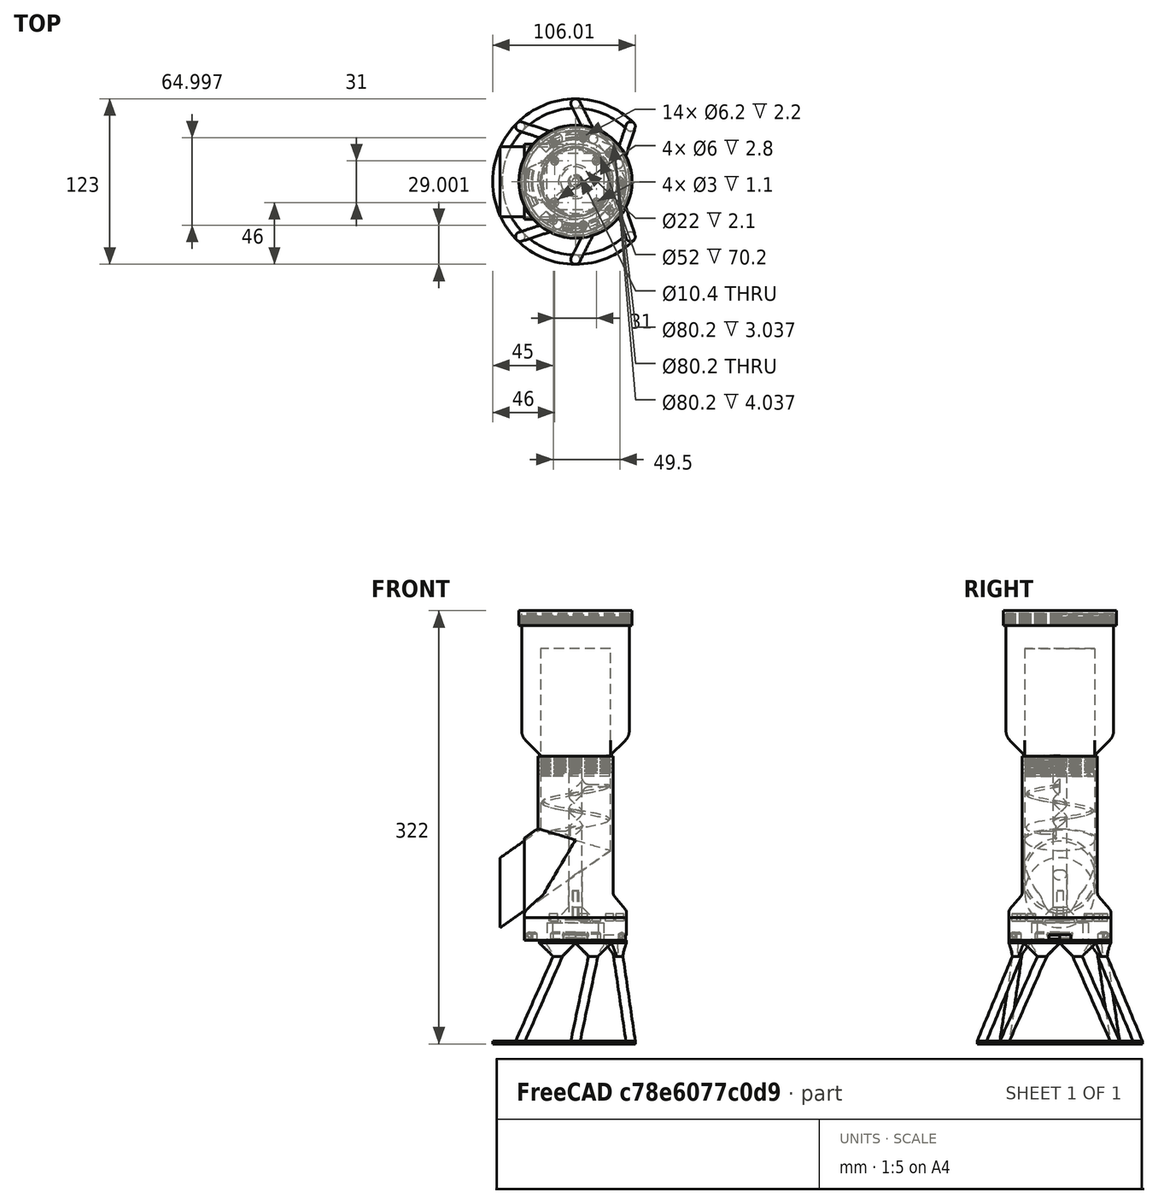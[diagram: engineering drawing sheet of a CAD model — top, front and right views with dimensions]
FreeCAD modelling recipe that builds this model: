
FCSTD DOCUMENT  (FreeCAD 1.0R38806 (Git))
Label: feeder
License: All rights reserved
LicenseURL: http://en.wikipedia.org/wiki/All_rights_reserved
objects: Sketcher::SketchObject×32, PartDesign::SubShapeBinder×25, PartDesign::Pocket×13, PartDesign::Pad×11, PartDesign::Body×8, PartDesign::PolarPattern×5, PartDesign::Revolution×4, PartDesign::Fillet×4, PartDesign::AdditiveHelix×3, PartDesign::Groove×3, PartDesign::SubtractiveHelix×2, Spreadsheet::Sheet×1, PartDesign::Mirrored×1, PartDesign::AdditiveLoft×1, PartDesign::MultiTransform×1, PartDesign::Boolean×1, PartDesign::Chamfer×1
note: 239 computed .brp shape members not serialized (recipe doc carries the construction recipe); baked Part::Feature solids carry a one-line shape summary decoded from their .brp

FEATURE [Spreadsheet::Sheet] Spreadsheet
  cells = A1='worm radius; B1(wormR)==25 mm; A2='wall thickness; B2(wallThickness)==2 mm; A3='worm wall gap; B3(wormWallGap)==1 mm; A4='tolerance; B4(tol)==0.1 mm; A5='shaft radius; B5(shaftR)==5 mm; A6='body radius; B6(bodyR)==wormR + wallThickness + wormWallGap; A7='worm Thickness; B7(wormThickness)==2 mm; A8='worm Smoothness; B8(wormSmoothness)==5 mm; A9='body height; B9(bodyH)==100 mm; A10='exit ratio; B10(exitRatio)=0.7; A11='worm Pitch; B11(wormPitch)==wormR; A12='legRadius; B12(legR)==5 mm; A13='motorMountHeight; B13(mountH)==17 mm; A14='container height; B14(containerH)==120 mm; A15='container radius; B15(containerR)==40 mm
FEATURE [Sketcher::SketchObject] Sketch  label="bodyProfile"
  ArcFitTolerance = 0
  AttachmentSupport = -> [XY_Plane]
  FullyConstrained = true
  MakeInternals = false
  MapMode = 5
  expr: Constraints[6] = Spreadsheet.wallThickness
  expr: Constraints[7] = Spreadsheet.wormR + Spreadsheet.wormWallGap
  sketch-geometry (3):
    g0: Circle CenterX=0 CenterY=0 CenterZ=0 NormalX=0 NormalY=0 NormalZ=1 AngleXU=0 Radius=26
    g1: Circle CenterX=0 CenterY=0 CenterZ=0 NormalX=0 NormalY=0 NormalZ=1 AngleXU=0 Radius=28
    g2: LineSegment [constr] StartX=26 StartY=0 StartZ=0 EndX=28 EndY=0 EndZ=0
  constraints (8):
    c: Coincident(g0,g-1)
    c: Coincident(g1,g0)
    c: PointOnObject(g2,g-1)
    c: PointOnObject(g2,g1)
    c: PointOnObject(g2,g0)
    c: PointOnObject(g2,g-1)
    c: DistanceX(g2,g2) = 2
    c: Radius(g0) = 26
FEATURE [Sketcher::SketchObject] Sketch001  label="wormProfile"
  ArcFitTolerance = 0
  AttachmentSupport = -> [XZ_Plane]
  FullyConstrained = true
  MakeInternals = false
  MapMode = 5
  Placement = pos=(0,0,0) rot=(1,0,0;1.5708rad)
  expr: Constraints[11] = Spreadsheet.wormSmoothness
  expr: Constraints[14] = Spreadsheet.wormR
  expr: Constraints[15] = Spreadsheet.wormThickness
  expr: Constraints[16] = Spreadsheet.shaftR - Spreadsheet.tol
  sketch-geometry (7):
    g0: ArcOfCircle CenterX=9.9 CenterY=6 CenterZ=0 NormalX=0 NormalY=0 NormalZ=1 AngleXU=0 Radius=5 StartAngle=3.1416 EndAngle=4.71239
    g1: LineSegment StartX=9.9 StartY=1 StartZ=0 EndX=24 EndY=1 EndZ=0
    g2: ArcOfCircle CenterX=24 CenterY=0 CenterZ=0 NormalX=0 NormalY=0 NormalZ=1 AngleXU=0 Radius=1 StartAngle=4.71239 EndAngle=7.85398
    g3: LineSegment StartX=24 StartY=-1 StartZ=0 EndX=9.9 EndY=-1 EndZ=0
    g4: ArcOfCircle CenterX=9.9 CenterY=-6 CenterZ=0 NormalX=0 NormalY=0 NormalZ=1 AngleXU=0 Radius=5 StartAngle=1.5708 EndAngle=3.14159
    g5: LineSegment StartX=4.9 StartY=5.99998 StartZ=0 EndX=4.9 EndY=-6 EndZ=0
    g6: GeomPoint [constr] X=25 Y=0 Z=0
  constraints (18):
    c: Horizontal(g1)
    c: Horizontal(g3)
    c: Coincident(g5,g0)
    c: Vertical(g5)
    c: Tangent(g5,g0)
    c: PointOnObject(g2,g-1)
    c: Tangent(g2,g1) = 1.5708
    c: Tangent(g3,g2) = 1.5708
    c: Tangent(g1,g0) = -1.5708
    c: Tangent(g4,g3) = -1.5708
    c: Equal(g0,g4)
    c: Radius(g0) = 5
    c: PointOnObject(g6,g2)
    c: PointOnObject(g6,g-1)
    c: DistanceX(g-1,g6) = 25
    c: DistanceY(g2,g1) = 2
    c: DistanceX(g-1,g0) = 4.9
    c: Tangent(g5,g4) = -1.5708
FEATURE [PartDesign::SubShapeBinder] Binder
  BindCopyOnChange = 0
  BindMode = 0
  ClaimChildren = false
  Context = -> Body001 [Binder.]
  Fuse = false
  MakeFace = true
  OffsetFill = false
  OffsetIntersection = false
  OffsetJoinType = 0
  OffsetOpenResult = false
  PartialLoad = false
  Relative = true
  Support = -> [Body[Sketch.Edge2]]
  _Version = 2
FEATURE [Sketcher::SketchObject] Sketch004  label="wormShaftProfile"
  ArcFitTolerance = 0
  AttachmentSupport = -> [XY_Plane]
  FullyConstrained = true
  MakeInternals = false
  MapMode = 5
  expr: Constraints[1] = Spreadsheet.shaftR
  expr: Constraints[7] = Spreadsheet.tol
  sketch-geometry (3):
    g0: Circle CenterX=0 CenterY=0 CenterZ=0 NormalX=0 NormalY=0 NormalZ=1 AngleXU=0 Radius=5
    g1: Circle CenterX=0 CenterY=0 CenterZ=0 NormalX=0 NormalY=0 NormalZ=1 AngleXU=0 Radius=5.1
    g2: LineSegment [constr] StartX=5 StartY=0 StartZ=0 EndX=5.1 EndY=0 EndZ=0
  constraints (8):
    c: Coincident(g0,g-1)
    c: Radius(g0) = 5
    c: Coincident(g1,g0)
    c: PointOnObject(g2,g0)
    c: PointOnObject(g2,g1)
    c: PointOnObject(g2,g-1)
    c: PointOnObject(g2,g-1)
    c: DistanceX(g2,g2) = 0.1
FEATURE [PartDesign::SubShapeBinder] Binder005
  BindCopyOnChange = 0
  BindMode = 0
  ClaimChildren = false
  Context = -> Body002 [Binder005.]
  Fuse = false
  MakeFace = true
  OffsetFill = false
  OffsetIntersection = false
  OffsetJoinType = 0
  OffsetOpenResult = false
  PartialLoad = false
  Placement = pos=(0,0,98) rot=(0,0,1;0rad)
  Relative = true
  Support = -> [Body[Sketch001.]]
  _Version = 2
  expr: .Placement.Base.z = Spreadsheet.bodyH + 10 mm - Spreadsheet.wormThickness - Spreadsheet.wormSmoothness - 5 mm
FEATURE [PartDesign::SubShapeBinder] Binder006
  BindCopyOnChange = 0
  BindMode = 0
  ClaimChildren = false
  Context = -> Body002 [Binder006.]
  Fuse = false
  MakeFace = true
  OffsetFill = false
  OffsetIntersection = false
  OffsetJoinType = 0
  OffsetOpenResult = false
  PartialLoad = false
  Relative = true
  Support = -> [Body[Sketch004.Edge1]]
  _Version = 2
FEATURE [PartDesign::Pad] Pad001
  Direction = (0,0,1)
  Length = 120
  Length2 = 10
  Profile = -> Binder006
  Suppressed = false
  Type = 0
  expr: Length = Spreadsheet.bodyH + 20 mm
FEATURE [PartDesign::AdditiveHelix] AdditiveHelix
  Angle = 0
  Axis = (1e-16,1e-16,1)
  Base = (0,0,0)
  BaseFeature = -> Pad001
  Growth = 0
  HasBeenEdited = true
  Height = 35
  LeftHanded = false
  Mode = 0
  Outside = false
  Pitch = 25
  Profile = -> Binder005 [Face1]
  ReferenceAxis = -> Z_Axis002
  Reversed = true
  Suppressed = false
  Turns = 1.4
  expr: Height = Spreadsheet.bodyH - 2 * Spreadsheet.bodyR - Spreadsheet.wormSmoothness - 2 * Spreadsheet.wormThickness
  expr: Pitch = Spreadsheet.wormPitch
FEATURE [Sketcher::SketchObject] Sketch073  label="Nema17"
  ArcFitTolerance = 0
  AttachmentSupport = -> [XY_Plane]
  FullyConstrained = true
  MakeInternals = false
  MapMode = 5
  sketch-geometry (21):
    g0: LineSegment StartX=-17 StartY=21.15 StartZ=0 EndX=17 EndY=21.15 EndZ=0
    g1: LineSegment StartX=17 StartY=21.15 StartZ=0 EndX=21.15 EndY=17 EndZ=0
    g2: LineSegment StartX=21.15 StartY=17 StartZ=0 EndX=21.15 EndY=-17 EndZ=0
    g3: LineSegment StartX=21.15 StartY=-17 StartZ=0 EndX=17 EndY=-21.15 EndZ=0
    g4: LineSegment StartX=17 StartY=-21.15 StartZ=0 EndX=-17 EndY=-21.15 EndZ=0
    g5: LineSegment StartX=-17 StartY=-21.15 StartZ=0 EndX=-21.15 EndY=-17 EndZ=0
    g6: LineSegment StartX=-21.15 StartY=-17 StartZ=0 EndX=-21.15 EndY=17 EndZ=0
    g7: LineSegment StartX=-21.15 StartY=17 StartZ=0 EndX=-17 EndY=21.15 EndZ=0
    g8: Circle CenterX=15.5 CenterY=15.5 CenterZ=0 NormalX=0 NormalY=0 NormalZ=1 AngleXU=0 Radius=1.5
    g9: Circle CenterX=-15.5 CenterY=15.5 CenterZ=0 NormalX=0 NormalY=0 NormalZ=1 AngleXU=0 Radius=1.5
    g10: Circle CenterX=-15.5 CenterY=-15.5 CenterZ=0 NormalX=0 NormalY=0 NormalZ=1 AngleXU=0 Radius=1.5
    g11: Circle CenterX=15.5 CenterY=-15.5 CenterZ=0 NormalX=0 NormalY=0 NormalZ=1 AngleXU=0 Radius=1.5
    g12: LineSegment [constr] StartX=-15.5 StartY=15.5 StartZ=0 EndX=-15.5 EndY=-15.5 EndZ=0
    g13: LineSegment [constr] StartX=-15.5 StartY=-15.5 StartZ=0 EndX=15.5 EndY=-15.5 EndZ=0
    g14: LineSegment [constr] StartX=15.5 StartY=-15.5 StartZ=0 EndX=15.5 EndY=15.5 EndZ=0
    g15: LineSegment [constr] StartX=15.5 StartY=15.5 StartZ=0 EndX=-15.5 EndY=15.5 EndZ=0
    g16: GeomPoint [constr] X=0 Y=0 Z=0
    g17: Circle CenterX=0 CenterY=0 CenterZ=0 NormalX=0 NormalY=0 NormalZ=1 AngleXU=0 Radius=11
    g18: Circle CenterX=0 CenterY=0 CenterZ=0 NormalX=0 NormalY=0 NormalZ=1 AngleXU=0 Radius=2.5
    g19: LineSegment StartX=-1.44513 StartY=-2.04 StartZ=0 EndX=1.44513 EndY=-2.04 EndZ=0
    g20: GeomPoint [constr] X=0 Y=2.5 Z=0
  constraints (48):
    c: Coincident(g0,g1)
    c: Coincident(g1,g2)
    c: Coincident(g2,g3)
    c: Coincident(g3,g4)
    c: Coincident(g4,g5)
    c: Coincident(g5,g6)
    c: Coincident(g6,g7)
    c: Coincident(g7,g0)
    c: Equal(g0,g6)
    c: DistanceX(g6,g1) = 42.3
    c: DistanceY(g4,g0) = 42.3
    c: Symmetric(g3,g0,g-1)
    c: Symmetric(g1,g2,g-1)
    c: Symmetric(g0,g0,g-2)
    c: Symmetric(g6,g1,g-2)
    c: DistanceX(g0,g0) = 34
    c: Symmetric(g2,g5,g-2)
    c: Symmetric(g3,g4,g-2)
    c: Coincident(g12,g13)
    c: Coincident(g13,g14)
    c: Coincident(g14,g15)
    c: Coincident(g15,g12)
    c: Horizontal(g13)
    c: Horizontal(g15)
    c: Vertical(g12)
    c: Vertical(g14)
    c: Symmetric(g13,g12,g16)
    c: Coincident(g16,g-1)
    c: Equal(g15,g14)
    c: DistanceX(g15,g15) = 31
    c: Coincident(g8,g14)
    c: Coincident(g9,g12)
    c: Coincident(g11,g13)
    c: Coincident(g10,g12)
    c: Equal(g8,g11)
    c: Equal(g11,g10)
    c: Equal(g10,g9)
    c: Diameter(g8) = 3
    c: Coincident(g17,g16)
    c: Coincident(g18,g17)
    c: Diameter(g17) = 22
    c: Diameter(g18) = 5
    c: PointOnObject(g19,g18)
    c: PointOnObject(g19,g18)
    c: Horizontal(g19)
    c: PointOnObject(g20,g18)
    c: PointOnObject(g20,g-2)
    c: DistanceY(g19,g20) = 4.54
FEATURE [PartDesign::SubShapeBinder] Binder021
  BindCopyOnChange = 0
  BindMode = 0
  ClaimChildren = false
  Context = -> Body005 [Binder021.]
  Fuse = false
  MakeFace = true
  OffsetFill = false
  OffsetIntersection = false
  OffsetJoinType = 0
  OffsetOpenResult = false
  PartialLoad = false
  Relative = true
  Support = -> [Body[Sketch073.]]
  _Version = 2
FEATURE [PartDesign::SubShapeBinder] Binder024
  BindCopyOnChange = 0
  BindMode = 0
  ClaimChildren = false
  Context = -> Body005 [Binder024.]
  Fuse = false
  MakeFace = true
  OffsetFill = false
  OffsetIntersection = false
  OffsetJoinType = 0
  OffsetOpenResult = false
  PartialLoad = false
  Placement = pos=(0,0,-2) rot=(0,0,1;0rad)
  Relative = true
  Support = -> [Binder021[Edge13]]
  _Version = 2
FEATURE [PartDesign::SubShapeBinder] Binder025
  BindCopyOnChange = 0
  BindMode = 0
  ClaimChildren = false
  Context = -> Body005 [Binder025.]
  Fuse = false
  MakeFace = true
  OffsetFill = false
  OffsetIntersection = false
  OffsetJoinType = 0
  OffsetOpenResult = false
  PartialLoad = false
  Placement = pos=(0,0,-4.1) rot=(0,0,1;0rad)
  Relative = true
  Support = -> [Binder021[Edge1,Edge7,Edge5,Edge3,Edge2,Edge8,Edge6,Edge4]]
  _Version = 2
FEATURE [Sketcher::SketchObject] Sketch081
  ArcFitTolerance = 0
  AttachmentSupport = -> [XY_Plane005]
  ExternalGeometry = -> [Binder021]
  FullyConstrained = true
  MakeInternals = false
  MapMode = 5
  sketch-geometry (1):
    g0: Circle CenterX=15.5 CenterY=15.5 CenterZ=0 NormalX=0 NormalY=0 NormalZ=1 AngleXU=0 Radius=3
  constraints (2):
    c: Coincident(g0,g-3)
    c: Diameter(g0) = 6
FEATURE [PartDesign::SubShapeBinder] Binder031
  BindCopyOnChange = 0
  BindMode = 0
  ClaimChildren = false
  Context = -> Body002 [Binder031.]
  Fuse = false
  MakeFace = true
  OffsetFill = false
  OffsetIntersection = false
  OffsetJoinType = 0
  OffsetOpenResult = false
  PartialLoad = false
  Relative = true
  Support = -> [Body[Sketch073.Edge14,Sketch073.Edge15]]
  _Version = 2
FEATURE [Sketcher::SketchObject] Sketch086
  ArcFitTolerance = 0
  FullyConstrained = false
  MakeInternals = false
  MapMode = 5
  expr: Constraints[4] = Spreadsheet.tol
  sketch-geometry (2):
    g0: Circle CenterX=0 CenterY=0 CenterZ=0 NormalX=0 NormalY=0 NormalZ=1 AngleXU=0 Radius=2.6
    g1: LineSegment [constr] StartX=2.5 StartY=0 StartZ=0 EndX=2.6 EndY=0 EndZ=0
  constraints (5):
    c: Coincident(g0,g-1)
    c: PointOnObject(g1,g0)
    c: PointOnObject(g1,g-1)
    c: PointOnObject(g1,g-1)
    c: DistanceX(g1,g1) = 0.1
FEATURE [PartDesign::Pocket] Pocket008
  BaseFeature = -> AdditiveHelix
  Direction = (0,0,-1)
  Length = 20
  Length2 = 5
  Profile = -> Sketch086
  ReferenceAxis = -> Sketch086 [N_Axis]
  Reversed = true
  Suppressed = false
  Type = 0
FEATURE [Sketcher::SketchObject] Sketch087
  ArcFitTolerance = 0
  FullyConstrained = false
  MakeInternals = false
  MapMode = 5
  sketch-geometry (2):
    g0: LineSegment StartX=-1.61196 StartY=-2.04 StartZ=0 EndX=1.61196 EndY=-2.04 EndZ=0
    g1: ArcOfCircle CenterX=0 CenterY=0 CenterZ=0 NormalX=0 NormalY=0 NormalZ=1 AngleXU=0 Radius=2.6 StartAngle=4.04367 EndAngle=5.38111
  constraints (3):
    c: Horizontal(g0)
    c: Coincident(g1,g0)
    c: Coincident(g0,g1)
FEATURE [PartDesign::Pad] Pad007
  BaseFeature = -> Pocket008
  Direction = (0,0,1)
  Length = 20
  Length2 = 10
  Profile = -> Sketch087
  ReferenceAxis = -> Sketch087 [N_Axis]
  Suppressed = false
  Type = 0
FEATURE [PartDesign::SubShapeBinder] Binder032
  BindCopyOnChange = 0
  BindMode = 0
  ClaimChildren = false
  Context = -> Body001 [Binder032.]
  Fuse = false
  MakeFace = true
  Offset = 0.1
  OffsetFill = false
  OffsetIntersection = false
  OffsetJoinType = 0
  OffsetOpenResult = false
  PartialLoad = false
  Relative = true
  Support = -> [Body[Sketch004.Edge2]]
  _Version = 2
FEATURE [PartDesign::SubShapeBinder] Binder033
  BindCopyOnChange = 0
  BindMode = 0
  ClaimChildren = false
  Context = -> Body001 [Binder033.]
  Fuse = false
  MakeFace = true
  OffsetFill = false
  OffsetIntersection = false
  OffsetJoinType = 0
  OffsetOpenResult = false
  PartialLoad = false
  Relative = true
  Support = -> [Body[Sketch083.Edge1,Sketch083.Edge2]]
  _Version = 2
FEATURE [Sketcher::SketchObject] Sketch088
  ArcFitTolerance = 0
  AttachmentSupport = -> [XZ_Plane001]
  FullyConstrained = false
  MakeInternals = false
  MapMode = 5
  Placement = pos=(0,0,0) rot=(1,0,0;1.5708rad)
  expr: Constraints[5] = Spreadsheet.tol
  sketch-geometry (4):
    g0: LineSegment StartX=0 StartY=12.6414 StartZ=0 EndX=12.6414 EndY=0 EndZ=0
    g1: LineSegment StartX=12.6414 StartY=0 StartZ=0 EndX=0 EndY=0 EndZ=0
    g2: LineSegment StartX=0 StartY=0 StartZ=0 EndX=0 EndY=12.6414 EndZ=0
    g3: LineSegment [constr] StartX=7.14853 StartY=5.35147 StartZ=0 EndX=7.21924 EndY=5.42218 EndZ=0
  constraints (9):
    c: PointOnObject(g0,g-1)
    c: Coincident(g1,g-1)
    c: Coincident(g1,g0)
    c: PointOnObject(g3,g0)
    c: Perpendicular(g0,g3)
    c: Distance(g3) = 0.1
    c: Coincident(g1,g2)
    c: PointOnObject(g0,g-2)
    c: Coincident(g2,g0)
FEATURE [Sketcher::SketchObject] Sketch095  label="containerScrew"
  ArcFitTolerance = 0
  AttachmentSupport = -> [XZ_Plane]
  FullyConstrained = false
  MakeInternals = false
  MapMode = 5
  Placement = pos=(0,0,0) rot=(1,0,0;1.5708rad)
  expr: Constraints[13] = 50 °
  expr: Constraints[16] = Spreadsheet.tol
  expr: Constraints[34] = Spreadsheet.tol
  expr: Constraints[3] = Spreadsheet.bodyH + 20 mm
  sketch-geometry (13):
    g0: LineSegment [constr] StartX=25.5 StartY=0 StartZ=0 EndX=25.5 EndY=120 EndZ=0
    g1: LineSegment [constr] StartX=27.5 StartY=0 StartZ=0 EndX=27.5 EndY=120 EndZ=0
    g2: LineSegment StartX=25.4 StartY=121 StartZ=0 EndX=26.4 EndY=120.161 EndZ=0
    g3: LineSegment StartX=26.4 StartY=120.161 StartZ=0 EndX=26.4 EndY=119.839 EndZ=0
    g4: LineSegment StartX=26.4 StartY=119.839 StartZ=0 EndX=25.4 EndY=119 EndZ=0
    g5: LineSegment StartX=25.4 StartY=121 StartZ=0 EndX=25.4 EndY=119 EndZ=0
    g6: LineSegment [constr] StartX=25.5 StartY=120 StartZ=0 EndX=0 EndY=120 EndZ=0
    g7: LineSegment StartX=25.2444 StartY=121 StartZ=0 EndX=25.2444 EndY=119 EndZ=0
    g8: LineSegment StartX=25.2444 StartY=121 StartZ=0 EndX=26.3 EndY=120.114 EndZ=0
    g9: LineSegment StartX=26.3 StartY=120.114 StartZ=0 EndX=26.3 EndY=119.886 EndZ=0
    g10: LineSegment StartX=26.3 StartY=119.886 StartZ=0 EndX=25.2444 EndY=119 EndZ=0
    g11: LineSegment [constr] StartX=26.3 StartY=120.114 StartZ=0 EndX=26.3643 EndY=120.191 EndZ=0
    g12: LineSegment [constr] StartX=26.3 StartY=120.114 StartZ=0 EndX=26.4 EndY=120.114 EndZ=0
  constraints (35):
    c: Vertical(g0)
    c: Vertical(g1)
    c: Equal(g1,g0)
    c: DistanceY(g0,g0) = 120
    c: Coincident(g3,g2)
    c: Coincident(g4,g3)
    c: Coincident(g5,g2)
    c: Coincident(g5,g4)
    c: Coincident(g6,g0)
    c: PointOnObject(g6,g-2)
    c: Horizontal(g6)
    c: Symmetric(g4,g2,g6)
    c: Symmetric(g2,g3,g6)
    c: Angle(g4,g5) = 0.872665
    c: DistanceY(g4,g2) = 2
    c: DistanceX(g2,g2) = 1
    c: DistanceX(g2,g0) = 0.1
    c: Coincident(g8,g7)
    c: Coincident(g10,g9)
    c: Coincident(g10,g7)
    c: Coincident(g9,g8)
    c: Parallel(g7,g5)
    c: Equal(g7,g5)
    c: Horizontal(g7,g2)
    c: Parallel(g10,g4)
    c: Parallel(g8,g2)
    c: Parallel(g9,g3)
    c: Coincident(g11,g8)
    c: PointOnObject(g11,g2)
    c: Coincident(g12,g8)
    c: PointOnObject(g12,g3)
    c: Perpendicular(g2,g11)
    c: Perpendicular(g3,g12)
    c: Equal(g12,g11)
    c: Distance(g12) = 0.1
FEATURE [Sketcher::SketchObject] Sketch096  label="containerProfile"
  ArcFitTolerance = 0
  AttachmentSupport = -> [XZ_Plane]
  FullyConstrained = false
  MakeInternals = false
  MapMode = 5
  Placement = pos=(0,0,0) rot=(1,0,0;1.5708rad)
  expr: Constraints[11] = Spreadsheet.tol
  expr: Constraints[12] = 15 mm
  expr: Constraints[13] = Spreadsheet.containerH
  expr: Constraints[15] = Spreadsheet.containerR
  expr: Constraints[1] = Spreadsheet.bodyH + 20 mm
  sketch-geometry (7):
    g0: LineSegment [constr] StartX=25.5 StartY=0 StartZ=0 EndX=25.5 EndY=120 EndZ=0
    g1: LineSegment StartX=25.4 StartY=105 StartZ=0 EndX=25.4 EndY=120 EndZ=0
    g2: LineSegment StartX=40 StartY=134.6 StartZ=0 EndX=40 EndY=225 EndZ=0
    g3: LineSegment StartX=40 StartY=225 StartZ=0 EndX=0 EndY=225 EndZ=0
    g4: LineSegment StartX=0 StartY=225 StartZ=0 EndX=0 EndY=105 EndZ=0
    g5: LineSegment StartX=0 StartY=105 StartZ=0 EndX=25.4 EndY=105 EndZ=0
    g6: LineSegment StartX=25.4 StartY=120 StartZ=0 EndX=40 EndY=134.6 EndZ=0
  constraints (20):
    c: Vertical(g0)
    c: DistanceY(g0,g0) = 120
    c: Vertical(g1)
    c: Vertical(g2)
    c: Coincident(g3,g2)
    c: PointOnObject(g4,g-2)
    c: PointOnObject(g4,g-2)
    c: Coincident(g5,g4)
    c: Horizontal(g5)
    c: Coincident(g1,g5)
    c: Horizontal(g0,g1)
    c: DistanceX(g1,g0) = 0.1
    c: DistanceY(g1,g1) = 15
    c: DistanceY(g4,g4) = 120
    c: Coincident(g4,g3)
    c: DistanceX(g3,g2) = 40
    c: Horizontal(g3)
    c: Coincident(g6,g1)
    c: Coincident(g6,g2)
    c: Angle(g2,g6) = 2.35619
FEATURE [PartDesign::SubShapeBinder] Binder036
  BindCopyOnChange = 0
  BindMode = 0
  ClaimChildren = false
  Context = -> Body007 [Binder036.]
  Fuse = false
  MakeFace = true
  OffsetFill = false
  OffsetIntersection = false
  OffsetJoinType = 0
  OffsetOpenResult = false
  PartialLoad = false
  Relative = true
  Support = -> [Body[Sketch096.]]
  _Version = 2
FEATURE [PartDesign::SubShapeBinder] Binder037
  BindCopyOnChange = 0
  BindMode = 0
  ClaimChildren = false
  Context = -> Body007 [Binder037.]
  Fuse = false
  MakeFace = true
  OffsetFill = false
  OffsetIntersection = false
  OffsetJoinType = 0
  OffsetOpenResult = false
  PartialLoad = false
  Relative = true
  Support = -> [Body[Sketch095.Edge5,Sketch095.Edge8,Sketch095.Edge7,Sketch095.Edge6]]
  _Version = 2
FEATURE [PartDesign::SubShapeBinder] Binder038
  BindCopyOnChange = 0
  BindMode = 0
  ClaimChildren = false
  Context = -> Body001 [Binder038.]
  Fuse = false
  MakeFace = true
  OffsetFill = false
  OffsetIntersection = false
  OffsetJoinType = 0
  OffsetOpenResult = false
  PartialLoad = false
  Relative = true
  Support = -> [Body[Sketch095.Edge2,Sketch095.Edge1,Sketch095.Edge3,Sketch095.Edge4]]
  _Version = 2
FEATURE [Sketcher::SketchObject] Sketch097  label="lidscrew"
  ArcFitTolerance = 0
  AttachmentSupport = -> [XZ_Plane]
  FullyConstrained = false
  MakeInternals = false
  MapMode = 5
  Placement = pos=(0,0,0) rot=(1,0,0;1.5708rad)
  expr: Constraints[23] = Spreadsheet.tol
  sketch-geometry (10):
    g0: LineSegment StartX=39.9 StartY=226 StartZ=0 EndX=40.9 EndY=225.161 EndZ=0
    g1: LineSegment StartX=40.9 StartY=225.161 StartZ=0 EndX=40.9 EndY=224.839 EndZ=0
    g2: LineSegment StartX=40.9 StartY=224.839 StartZ=0 EndX=39.9 EndY=224 EndZ=0
    g3: LineSegment StartX=39.9 StartY=224 StartZ=0 EndX=39.9 EndY=226 EndZ=0
    g4: LineSegment StartX=40.0556 StartY=224 StartZ=0 EndX=40.0556 EndY=226 EndZ=0
    g5: LineSegment StartX=40.0556 StartY=226 StartZ=0 EndX=41 EndY=225.208 EndZ=0
    g6: LineSegment StartX=41 StartY=225.208 StartZ=0 EndX=41 EndY=224.792 EndZ=0
    g7: LineSegment StartX=41 StartY=224.792 StartZ=0 EndX=40.0556 EndY=224 EndZ=0
    g8: LineSegment [constr] StartX=40.9 StartY=225.161 StartZ=0 EndX=40.9643 EndY=225.238 EndZ=0
    g9: LineSegment [constr] StartX=40.9 StartY=225.161 StartZ=0 EndX=41 EndY=225.161 EndZ=0
  constraints (25):
    c: Coincident(g1,g0)
    c: Coincident(g3,g0)
    c: Coincident(g3,g2)
    c: Coincident(g1,g2)
    c: Angle(g2,g3) = 0.872665
    c: DistanceY(g2,g0) = 2
    c: DistanceX(g0,g0) = 1
    c: Coincident(g5,g4)
    c: Coincident(g6,g5)
    c: Coincident(g7,g6)
    c: Coincident(g7,g4)
    c: Parallel(g4,g3)
    c: Parallel(g5,g0)
    c: Parallel(g2,g7)
    c: Parallel(g6,g1)
    c: Coincident(g8,g0)
    c: PointOnObject(g8,g5)
    c: Coincident(g9,g0)
    c: PointOnObject(g9,g6)
    c: Perpendicular(g6,g9)
    c: Perpendicular(g5,g8)
    c: Equal(g9,g8)
    c: Equal(g4,g3)
    c: Distance(g9) = 0.1
    c: Horizontal(g4,g0)
FEATURE [PartDesign::SubShapeBinder] Binder039
  BindCopyOnChange = 0
  BindMode = 0
  ClaimChildren = false
  Context = -> Body007 [Binder039.]
  Fuse = false
  MakeFace = true
  OffsetFill = false
  OffsetIntersection = false
  OffsetJoinType = 0
  OffsetOpenResult = false
  PartialLoad = false
  Placement = pos=(0,0,-1) rot=(0,0,1;0rad)
  Relative = true
  Support = -> [Body[Sketch097.Edge4,Sketch097.Edge1,Sketch097.Edge2,Sketch097.Edge3]]
  _Version = 2
FEATURE [PartDesign::SubShapeBinder] Binder040
  BindCopyOnChange = 0
  BindMode = 0
  ClaimChildren = false
  Context = -> Body008 [Binder040.]
  Fuse = false
  MakeFace = true
  OffsetFill = false
  OffsetIntersection = false
  OffsetJoinType = 0
  OffsetOpenResult = false
  PartialLoad = false
  Relative = true
  Support = -> [Body[Sketch096.Edge4]]
  _Version = 2
FEATURE [PartDesign::SubShapeBinder] Binder041
  BindCopyOnChange = 0
  BindMode = 0
  ClaimChildren = false
  Context = -> Body008 [Binder041.]
  Fuse = false
  MakeFace = true
  OffsetFill = false
  OffsetIntersection = false
  OffsetJoinType = 0
  OffsetOpenResult = false
  PartialLoad = false
  Relative = true
  Support = -> [Body[Sketch097.Edge6,Sketch097.Edge7,Sketch097.Edge8,Sketch097.Edge5]]
  _Version = 2
FEATURE [Sketcher::SketchObject] Sketch098
  ArcFitTolerance = 0
  FullyConstrained = false
  MakeInternals = false
  MapMode = 5
  Placement = pos=(0,0,0) rot=(1,0,0;1.5708rad)
  expr: Constraints[13] = 2 mm
  sketch-geometry (6):
    g0: LineSegment StartX=0 StartY=226 StartZ=0 EndX=40.1 EndY=226 EndZ=0
    g1: LineSegment StartX=40.1 StartY=226 StartZ=0 EndX=40.1 EndY=217 EndZ=0
    g2: LineSegment StartX=40.1 StartY=217 StartZ=0 EndX=42.1 EndY=217 EndZ=0
    g3: LineSegment StartX=42.1 StartY=217 StartZ=0 EndX=42.1 EndY=228 EndZ=0
    g4: LineSegment StartX=42.1 StartY=228 StartZ=0 EndX=0 EndY=228 EndZ=0
    g5: LineSegment StartX=0 StartY=228 StartZ=0 EndX=0 EndY=226 EndZ=0
  constraints (16):
    c: Horizontal(g0)
    c: Vertical(g1)
    c: Coincident(g2,g1)
    c: Horizontal(g2)
    c: Vertical(g3)
    c: Horizontal(g4)
    c: Coincident(g5,g0)
    c: Coincident(g5,g4)
    c: Equal(g2,g5)
    c: Coincident(g1,g0)
    c: Coincident(g2,g3)
    c: Coincident(g3,g4)
    c: Vertical(g5)
    c: DistanceX(g2,g2) = 2
    c: PointOnObject(g4,g-2)
    c: DistanceY(g1,g0) = 9
FEATURE [PartDesign::Revolution] Revolution002
  Angle = 360
  Angle2 = 60
  Axis = (0,2e-16,1)
  Base = (0,0,0)
  Placement = pos=(0,0,0) rot=(1,0,0;1.5708rad)
  Profile = -> Sketch098
  ReferenceAxis = -> Sketch098 [V_Axis]
  Reversed = true
  Suppressed = false
  Type = 0
FEATURE [PartDesign::SubtractiveHelix] SubtractiveHelix002
  Angle = 0
  Axis = (1e-16,1e-16,1)
  Base = (0,0,0)
  BaseFeature = -> Revolution002
  Growth = 0
  HasBeenEdited = true
  Height = 9
  LeftHanded = false
  Mode = 0
  Outside = false
  Pitch = 3
  Placement = pos=(0,0,0) rot=(1,0,0;1.5708rad)
  Profile = -> Binder041 [Face1]
  ReferenceAxis = -> Z_Axis008
  Reversed = true
  Suppressed = false
  Turns = 3
FEATURE [PartDesign::Body] Body008  label="lid"
  AllowCompound = false
  Group = -> [Binder040,Binder041,Sketch098,Revolution002,SubtractiveHelix002]
  Origin = -> Origin008
  Tip = -> SubtractiveHelix002
FEATURE [Sketcher::SketchObject] Sketch103  label="holeProfile"
  ArcFitTolerance = 0
  AttachmentOffset = pos=(0,0,-28) rot=(0,0,1;0rad)
  AttachmentSupport = -> [YZ_Plane]
  FullyConstrained = true
  MakeInternals = false
  MapMode = 5
  Placement = pos=(-28,0,0) rot=(0.57735,0.57735,0.57735;2.0944rad)
  expr: .AttachmentOffset.Base.z = -Spreadsheet.bodyR
  expr: .Placement.Base.x = -Spreadsheet.bodyR
  expr: Constraints[1] = Spreadsheet.wallThickness + 10 mm
  expr: Constraints[2] = Spreadsheet.bodyR - Spreadsheet.wallThickness
  sketch-geometry (2):
    g0: GeomPoint [constr] X=0 Y=12 Z=0
    g1: Circle CenterX=0 CenterY=38 CenterZ=0 NormalX=0 NormalY=0 NormalZ=1 AngleXU=0 Radius=26
  constraints (5):
    c: PointOnObject(g0,g-2)
    c: DistanceY(g-1,g0) = 12
    c: Radius(g1) = 26
    c: PointOnObject(g0,g1)
    c: PointOnObject(g1,g-2)
FEATURE [PartDesign::Revolution] Revolution
  Angle = 360
  Angle2 = 60
  Axis = (1e-16,1e-16,1)
  Base = (0,0,0)
  Profile = -> Binder036 [Face1]
  ReferenceAxis = -> Z_Axis007
  Refine = true
  Reversed = true
  Suppressed = false
  Type = 0
FEATURE [PartDesign::AdditiveHelix] AdditiveHelix002
  Angle = 0
  Axis = (1e-16,1e-16,1)
  Base = (0,0,0)
  BaseFeature = -> Revolution
  Growth = 0
  HasBeenEdited = true
  Height = 14
  LeftHanded = false
  Mode = 0
  Outside = false
  Pitch = 3
  Profile = -> Binder037 [Face1]
  ReferenceAxis = -> Z_Axis007
  Reversed = true
  Suppressed = false
  Turns = 4.66667
FEATURE [PartDesign::AdditiveHelix] AdditiveHelix003
  Angle = 0
  Axis = (1e-16,1e-16,1)
  Base = (0,0,0)
  BaseFeature = -> AdditiveHelix002
  Growth = 0
  HasBeenEdited = true
  Height = 6
  LeftHanded = false
  Mode = 0
  Outside = false
  Pitch = 3
  Profile = -> Binder039 [Face1]
  ReferenceAxis = -> Z_Axis007
  Reversed = true
  Suppressed = false
  Turns = 2
FEATURE [PartDesign::Fillet] Fillet002
  Base = -> AdditiveHelix003 [Edge49]
  BaseFeature = -> AdditiveHelix003
  Radius = 10
  SupportTransform = false
  Suppressed = false
  UseAllEdges = false
FEATURE [PartDesign::Body] Body007  label="container"
  AllowCompound = false
  Group = -> [Binder036,Revolution,Binder037,AdditiveHelix002,Binder039,AdditiveHelix003,Fillet002]
  Origin = -> Origin007
  Tip = -> Fillet002
FEATURE [PartDesign::SubShapeBinder] Binder058
  BindCopyOnChange = 0
  BindMode = 0
  ClaimChildren = false
  Context = -> Body012 [Binder058.]
  Fuse = false
  MakeFace = true
  OffsetFill = false
  OffsetIntersection = false
  OffsetJoinType = 0
  OffsetOpenResult = false
  PartialLoad = false
  Refine = true
  Relative = true
  Support = -> [Body[Sketch103.]]
  _Version = 2
FEATURE [PartDesign::SubShapeBinder] Binder060
  BindCopyOnChange = 0
  BindMode = 0
  ClaimChildren = false
  Context = -> Body001 [Binder060.]
  Fuse = false
  MakeFace = true
  OffsetFill = false
  OffsetIntersection = false
  OffsetJoinType = 0
  OffsetOpenResult = false
  PartialLoad = false
  Refine = true
  Relative = true
  Support = -> [Body012]
  _Version = 2
FEATURE [Sketcher::SketchObject] Sketch112
  ArcFitTolerance = 0
  AttachmentSupport = -> [YZ_Plane005]
  FullyConstrained = true
  MakeInternals = false
  MapMode = 5
  Placement = pos=(0,0,0) rot=(0.57735,0.57735,0.57735;2.0944rad)
  expr: Constraints[10] = Spreadsheet.mountH - 4.1 mm + Spreadsheet.tol
  expr: Constraints[8] = Spreadsheet.mountH
  sketch-geometry (4):
    g0: LineSegment StartX=-8.1 StartY=-17 StartZ=0 EndX=8.1 EndY=-17 EndZ=0
    g1: LineSegment StartX=8.1 StartY=-17 StartZ=0 EndX=8.1 EndY=-13 EndZ=0
    g2: LineSegment StartX=8.1 StartY=-13 StartZ=0 EndX=-8.1 EndY=-13 EndZ=0
    g3: LineSegment StartX=-8.1 StartY=-13 StartZ=0 EndX=-8.1 EndY=-17 EndZ=0
  constraints (11):
    c: Coincident(g0,g1)
    c: Coincident(g1,g2)
    c: Coincident(g2,g3)
    c: Coincident(g3,g0)
    c: Horizontal(g2)
    c: Vertical(g1)
    c: Vertical(g3)
    c: Symmetric(g0,g0,g-2)
    c: DistanceY(g0,g-1) = 17
    c: DistanceX(g0,g0) = 16.2
    c: DistanceY(g1,g-1) = 13
FEATURE [Sketcher::SketchObject] Sketch114  label="motorMountProfile"
  ArcFitTolerance = 0
  AttachmentSupport = -> [XY_Plane]
  ExternalGeometry = -> [Sketch]
  FullyConstrained = true
  MakeInternals = false
  MapMode = 5
  sketch-geometry (2):
    g0: Circle CenterX=0 CenterY=0 CenterZ=0 NormalX=0 NormalY=0 NormalZ=1 AngleXU=0 Radius=38
    g1: LineSegment [constr] StartX=28 StartY=0 StartZ=0 EndX=38 EndY=0 EndZ=0
  constraints (6):
    c: Coincident(g0,g-1)
    c: PointOnObject(g1,g-1)
    c: PointOnObject(g1,g0)
    c: Horizontal(g1)
    c: PointOnObject(g1,g-3)
    c: DistanceX(g1,g1) = 10
FEATURE [PartDesign::SubShapeBinder] Binder066
  BindCopyOnChange = 0
  BindMode = 0
  ClaimChildren = false
  Context = -> Body001 [Binder066.]
  Fuse = false
  MakeFace = false
  OffsetFill = false
  OffsetIntersection = false
  OffsetJoinType = 0
  OffsetOpenResult = false
  PartialLoad = false
  Refine = true
  Relative = true
  Support = -> [Body[Sketch114.]]
  _Version = 2
FEATURE [PartDesign::SubShapeBinder] Binder067
  BindCopyOnChange = 0
  BindMode = 0
  ClaimChildren = false
  Context = -> Body005 [Binder067.]
  Fuse = false
  MakeFace = true
  OffsetFill = false
  OffsetIntersection = false
  OffsetJoinType = 0
  OffsetOpenResult = false
  PartialLoad = false
  Refine = true
  Relative = true
  Support = -> [Body[Sketch114.]]
  _Version = 2
FEATURE [PartDesign::Pad] Pad021
  Direction = (0,0,1)
  Length = 17
  Length2 = 10
  Profile = -> Binder067
  Refine = true
  Reversed = true
  Suppressed = false
  Type = 0
  expr: Length = Spreadsheet.mountH
FEATURE [Sketcher::SketchObject] Sketch116
  ArcFitTolerance = 0
  AttachmentSupport = -> [XY_Plane005]
  ExternalGeometry = -> [Binder021]
  FullyConstrained = true
  MakeInternals = false
  MapMode = 5
  sketch-geometry (1):
    g0: Circle CenterX=0 CenterY=0 CenterZ=0 NormalX=0 NormalY=0 NormalZ=1 AngleXU=0 Radius=2.5
  constraints (2):
    c: Coincident(g0,g-1)
    c: Equal(g0,g-3)
FEATURE [Sketcher::SketchObject] Sketch117  label="magnetProfile"
  ArcFitTolerance = 0
  AttachmentSupport = -> [XY_Plane]
  ExternalGeometry = -> [Sketch114,Sketch]
  FullyConstrained = true
  MakeInternals = false
  MapMode = 5
  sketch-geometry (14):
    g0: Circle CenterX=33 CenterY=0 CenterZ=0 NormalX=0 NormalY=0 NormalZ=1 AngleXU=0 Radius=3.1
    g1: LineSegment [constr] StartX=28 StartY=0 StartZ=0 EndX=33 EndY=0 EndZ=0
    g2: LineSegment [constr] StartX=33 StartY=0 StartZ=0 EndX=38 EndY=0 EndZ=0
    g3: Circle [constr] CenterX=0 CenterY=0 CenterZ=0 NormalX=0 NormalY=0 NormalZ=1 AngleXU=0 Radius=33
    g4: Circle CenterX=-16.5 CenterY=28.5788 CenterZ=0 NormalX=0 NormalY=0 NormalZ=1 AngleXU=0 Radius=3.1
    g5: Circle CenterX=5.73039 CenterY=32.4987 CenterZ=0 NormalX=0 NormalY=0 NormalZ=1 AngleXU=0 Radius=3.1
    g6: Circle CenterX=25.2795 CenterY=21.212 CenterZ=0 NormalX=0 NormalY=0 NormalZ=1 AngleXU=0 Radius=3.1
    g7: Circle CenterX=25.2795 CenterY=-21.212 CenterZ=0 NormalX=0 NormalY=0 NormalZ=1 AngleXU=0 Radius=3.1
    g8: Circle CenterX=5.73039 CenterY=-32.4987 CenterZ=0 NormalX=0 NormalY=0 NormalZ=1 AngleXU=0 Radius=3.1
    g9: Circle CenterX=-16.5 CenterY=-28.5788 CenterZ=0 NormalX=0 NormalY=0 NormalZ=1 AngleXU=0 Radius=3.1
    g10: LineSegment [constr] StartX=-16.5 StartY=28.5788 StartZ=0 EndX=0 EndY=0 EndZ=0
    g11: LineSegment [constr] StartX=-16.5 StartY=28.5788 StartZ=0 EndX=5.73039 EndY=32.4987 EndZ=0
    g12: LineSegment [constr] StartX=5.73039 StartY=32.4987 StartZ=0 EndX=25.2795 EndY=21.212 EndZ=0
    g13: LineSegment [constr] StartX=25.2795 StartY=21.212 StartZ=0 EndX=33 EndY=0 EndZ=0
  constraints (34):
    c: PointOnObject(g0,g-1)
    c: PointOnObject(g1,g-4)
    c: Coincident(g1,g0)
    c: Horizontal(g1)
    c: Coincident(g2,g0)
    c: PointOnObject(g2,g-3)
    c: Horizontal(g2)
    c: Equal(g1,g2)
    c: Diameter(g0) = 6.2
    c: Coincident(g3,g-1)
    c: PointOnObject(g0,g3)
    c: PointOnObject(g4,g3)
    c: PointOnObject(g5,g3)
    c: PointOnObject(g6,g3)
    c: Coincident(g10,g4)
    c: Coincident(g10,g3)
    c: Angle(g-1,g10) = 2.0944
    c: Coincident(g11,g4)
    c: Coincident(g11,g5)
    c: Coincident(g12,g5)
    c: Coincident(g12,g6)
    c: Coincident(g13,g6)
    c: Coincident(g13,g0)
    c: Equal(g13,g12)
    c: Equal(g12,g11)
    c: Equal(g0,g6)
    c: Equal(g6,g5)
    c: Equal(g5,g4)
    c: Equal(g4,g7)
    c: Equal(g7,g8)
    c: Equal(g8,g9)
    c: Symmetric(g9,g4,g-1)
    c: Symmetric(g8,g5,g-1)
    c: Symmetric(g7,g6,g-1)
FEATURE [PartDesign::Body] Body  label="sketches"
  AllowCompound = false
  Group = -> [Sketch,Sketch001,Sketch004,Sketch073,Sketch095,Sketch096,Sketch097,Sketch103,Sketch114,Sketch117]
  Origin = -> Origin
FEATURE [PartDesign::SubShapeBinder] Binder068
  BindCopyOnChange = 0
  BindMode = 0
  ClaimChildren = false
  Context = -> Body001 [Binder068.]
  Fuse = false
  MakeFace = true
  OffsetFill = false
  OffsetIntersection = false
  OffsetJoinType = 0
  OffsetOpenResult = false
  PartialLoad = false
  Placement = pos=(0,0,0.6) rot=(0,0,1;0rad)
  Refine = true
  Relative = true
  Support = -> [Body[Sketch117.]]
  _Version = 2
FEATURE [Sketcher::SketchObject] Sketch118
  ArcFitTolerance = 0
  AttachmentSupport = -> [YZ_Plane001]
  ExternalGeometry = -> [Binder]
  FullyConstrained = true
  MakeInternals = false
  MapMode = 5
  Placement = pos=(0,0,0) rot=(0.57735,0.57735,0.57735;2.0944rad)
  expr: Constraints[12] = Spreadsheet.bodyH + 20 mm
  sketch-geometry (6):
    g0: LineSegment StartX=0 StartY=0 StartZ=0 EndX=38 EndY=0 EndZ=0
    g1: LineSegment StartX=38 StartY=5 StartZ=0 EndX=28 EndY=16.9175 EndZ=0
    g2: LineSegment StartX=28 StartY=16.9175 StartZ=0 EndX=28 EndY=120 EndZ=0
    g3: LineSegment StartX=28 StartY=120 StartZ=0 EndX=0 EndY=120 EndZ=0
    g4: LineSegment StartX=0 StartY=120 StartZ=0 EndX=0 EndY=0 EndZ=0
    g5: LineSegment StartX=38 StartY=5 StartZ=0 EndX=38 EndY=0 EndZ=0
  constraints (17):
    c: Coincident(g0,g-1)
    c: PointOnObject(g0,g-1)
    c: Coincident(g2,g1)
    c: Vertical(g2)
    c: Coincident(g3,g2)
    c: PointOnObject(g3,g-2)
    c: Horizontal(g3)
    c: Coincident(g4,g3)
    c: Coincident(g4,g0)
    c: Coincident(g5,g1)
    c: Coincident(g5,g0)
    c: Vertical(g5)
    c: DistanceY(g0,g3) = 120
    c: Vertical(g2,g-3)
    c: DistanceX(g-3,g0) = 10
    c: DistanceY(g0,g1) = 5
    c: Angle(g4,g1) = 0.698132
FEATURE [PartDesign::Revolution] Revolution004
  Angle = 360
  Angle2 = 60
  Axis = (1e-16,1e-16,1)
  Base = (0,0,0)
  Placement = pos=(0,0,0) rot=(1,1,1;2.0944rad)
  Profile = -> Sketch118
  ReferenceAxis = -> Z_Axis001
  Reversed = true
  Suppressed = false
  Type = 0
FEATURE [PartDesign::SubShapeBinder] Binder069
  BindCopyOnChange = 0
  BindMode = 0
  ClaimChildren = false
  Context = -> Body005 [Binder069.]
  Fuse = false
  MakeFace = true
  OffsetFill = false
  OffsetIntersection = false
  OffsetJoinType = 0
  OffsetOpenResult = false
  PartialLoad = false
  Placement = pos=(0,0,-0.6) rot=(0,0,1;0rad)
  Relative = true
  Support = -> [Body[Sketch117.]]
  _Version = 2
FEATURE [PartDesign::SubShapeBinder] Binder070
  BindCopyOnChange = 0
  BindMode = 0
  ClaimChildren = false
  Context = -> Body012 [Binder070.]
  Fuse = false
  MakeFace = true
  OffsetFill = false
  OffsetIntersection = false
  OffsetJoinType = 0
  OffsetOpenResult = false
  PartialLoad = false
  Relative = true
  Support = -> [Body[Sketch.Edge1]]
  _Version = 2
FEATURE [PartDesign::Pad] Pad024
  Direction = (0,0,1)
  Length = 200
  Length2 = 10
  Profile = -> Binder070 [Face1]
  Suppressed = false
  Type = 0
  expr: Length = 2 * Spreadsheet.bodyH
FEATURE [Sketcher::SketchObject] Sketch122
  ArcFitTolerance = 0
  AttachmentOffset = pos=(0,0,-28) rot=(0,0,1;0rad)
  AttachmentSupport = -> [YZ_Plane013]
  ExternalGeometry = -> [Binder058]
  FullyConstrained = true
  MakeInternals = false
  MapMode = 5
  Placement = pos=(-28,0,0) rot=(0.57735,0.57735,0.57735;2.0944rad)
  expr: .AttachmentOffset.Base.z = -Spreadsheet.bodyR
  expr: Constraints[5] = Spreadsheet.bodyH
  sketch-geometry (6):
    g0: LineSegment StartX=-76 StartY=38 StartZ=0 EndX=-76 EndY=-62 EndZ=0
    g1: LineSegment StartX=-76 StartY=-62 StartZ=0 EndX=76 EndY=-62 EndZ=0
    g2: LineSegment StartX=76 StartY=-62 StartZ=0 EndX=76 EndY=38 EndZ=0
    g3: ArcOfCircle CenterX=0 CenterY=38 CenterZ=0 NormalX=0 NormalY=0 NormalZ=1 AngleXU=0 Radius=26 StartAngle=3.14159 EndAngle=6.28319
    g4: LineSegment StartX=-76 StartY=38 StartZ=0 EndX=-26 EndY=38 EndZ=0
    g5: LineSegment StartX=26 StartY=38 StartZ=0 EndX=76 EndY=38 EndZ=0
  constraints (18):
    c: Vertical(g0)
    c: Coincident(g1,g0)
    c: Horizontal(g1)
    c: Coincident(g2,g1)
    c: Vertical(g2)
    c: DistanceY(g2,g2) = 100
    c: Horizontal(g3,g3)
    c: Horizontal(g3,g3)
    c: Coincident(g4,g0)
    c: Coincident(g4,g3)
    c: Horizontal(g4)
    c: Coincident(g5,g3)
    c: Coincident(g5,g2)
    c: Horizontal(g5)
    c: Equal(g5,g4)
    c: DistanceX(g5,g5) = 50
    c: Coincident(g3,g-3)
    c: Equal(g-3,g3)
FEATURE [Sketcher::SketchObject] Sketch123
  ArcFitTolerance = 0
  ExternalGeometry = -> [Binder067]
  FullyConstrained = true
  MakeInternals = false
  MapMode = 5
  Placement = pos=(0,0,0) rot=(0.57735,0.57735,0.57735;2.0944rad)
  expr: Constraints[2] = Spreadsheet.mountH
  sketch-geometry (12):
    g0: LineSegment [constr] StartX=35 StartY=0 StartZ=0 EndX=35 EndY=-17 EndZ=0
    g1: LineSegment StartX=35 StartY=-15.1547 StartZ=0 EndX=37 EndY=-13.1547 EndZ=0
    g2: LineSegment StartX=37 StartY=-13.1547 StartZ=0 EndX=37 EndY=-12.1547 EndZ=0
    g3: LineSegment StartX=33 StartY=-17 StartZ=0 EndX=35 EndY=-17 EndZ=0
    g4: LineSegment StartX=33 StartY=-17 StartZ=0 EndX=32 EndY=-17 EndZ=0
    g5: LineSegment StartX=33 StartY=-16 StartZ=0 EndX=32 EndY=-17 EndZ=0
    g6: LineSegment StartX=33 StartY=-16 StartZ=0 EndX=33 EndY=-12.1547 EndZ=0
    g7: LineSegment StartX=33 StartY=-12.1547 StartZ=0 EndX=35 EndY=-11 EndZ=0
    g8: LineSegment StartX=35 StartY=-11 StartZ=0 EndX=37 EndY=-12.1547 EndZ=0
    g9: LineSegment StartX=36 StartY=-17 StartZ=0 EndX=35 EndY=-16 EndZ=0
    g10: LineSegment StartX=35 StartY=-16 StartZ=0 EndX=35 EndY=-15.1547 EndZ=0
    g11: LineSegment StartX=35 StartY=-17 StartZ=0 EndX=36 EndY=-17 EndZ=0
  constraints (36):
    c: PointOnObject(g0,g-1)
    c: Vertical(g0)
    c: DistanceY(g0,g0) = 17
    c: PointOnObject(g1,g0)
    c: Coincident(g1,g2)
    c: Vertical(g2)
    c: Coincident(g3,g0)
    c: Horizontal(g3)
    c: Angle(g1) = 0.785398
    c: Coincident(g4,g3)
    c: Horizontal(g4)
    c: Coincident(g5,g4)
    c: Coincident(g6,g5)
    c: Vertical(g6)
    c: Coincident(g7,g6)
    c: PointOnObject(g7,g0)
    c: Coincident(g8,g7)
    c: Coincident(g8,g2)
    c: PointOnObject(g9,g0)
    c: Coincident(g10,g9)
    c: Coincident(g10,g1)
    c: Coincident(g11,g0)
    c: Horizontal(g9,g5)
    c: Angle(g9,g11) = 0.785398
    c: Coincident(g11,g9)
    c: Horizontal(g11)
    c: Equal(g9,g5)
    c: Horizontal(g2,g6)
    c: Angle(g3,g7) = 0.523599
    c: Equal(g8,g7)
    c: Vertical(g3,g5)
    c: DistanceX(g5,g9) = 2
    c: DistanceX(g4,g3) = 1
    c: DistanceY(g1,g2) = 1
    c: DistanceY(g0,g7) = 6
    c: DistanceX(g2,g-3) = 1
FEATURE [Sketcher::SketchObject] Sketch124
  ArcFitTolerance = 0
  ExternalGeometry = -> [Sketch123]
  FullyConstrained = true
  MakeInternals = false
  MapMode = 5
  Placement = pos=(0,0,0) rot=(0.57735,0.57735,0.57735;2.0944rad)
  sketch-geometry (7):
    g0: LineSegment StartX=32 StartY=-17 StartZ=0 EndX=33 EndY=-16 EndZ=0
    g1: LineSegment StartX=33 StartY=-16 StartZ=0 EndX=33 EndY=-12.1547 EndZ=0
    g2: LineSegment StartX=33 StartY=-12.1547 StartZ=0 EndX=35 EndY=-11 EndZ=0
    g3: LineSegment StartX=35 StartY=-11 StartZ=0 EndX=37 EndY=-12.1547 EndZ=0
    g4: LineSegment StartX=37 StartY=-12.1547 StartZ=0 EndX=37 EndY=-16 EndZ=0
    g5: LineSegment StartX=37 StartY=-16 StartZ=0 EndX=38 EndY=-17 EndZ=0
    g6: LineSegment StartX=38 StartY=-17 StartZ=0 EndX=32 EndY=-17 EndZ=0
  constraints (16):
    c: Coincident(g-6,g0)
    c: Coincident(g0,g-6)
    c: Coincident(g0,g1)
    c: Coincident(g1,g-5)
    c: Coincident(g1,g2)
    c: Coincident(g2,g-4)
    c: Coincident(g2,g3)
    c: Coincident(g3,g-7)
    c: Coincident(g3,g4)
    c: Vertical(g4)
    c: Coincident(g4,g5)
    c: Coincident(g5,g6)
    c: Coincident(g6,g0)
    c: Horizontal(g6)
    c: Equal(g5,g0)
    c: Angle(g5,g6) = 0.785398
FEATURE [Sketcher::SketchObject] Sketch125
  ArcFitTolerance = 0
  AttachmentOffset = pos=(0,0,-17) rot=(0,0,1;0rad)
  AttachmentSupport = -> [XY_Plane005]
  ExternalGeometry = -> [Sketch123]
  FullyConstrained = true
  MakeInternals = false
  MapMode = 5
  Placement = pos=(0,0,-17) rot=(0,0,1;0rad)
  expr: .AttachmentOffset.Base.z = -Spreadsheet.mountH
  sketch-geometry (4):
    g0: Circle [constr] CenterX=0 CenterY=0 CenterZ=0 NormalX=0 NormalY=0 NormalZ=1 AngleXU=0 Radius=37
    g1: LineSegment [constr] StartX=0 StartY=37 StartZ=0 EndX=0 EndY=0 EndZ=0
    g2: LineSegment [constr] StartX=0 StartY=0 StartZ=0 EndX=4.82947 EndY=36.6835 EndZ=0
    g3: Circle CenterX=4.85557 CenterY=36.8817 CenterZ=0 NormalX=0 NormalY=0 NormalZ=1 AngleXU=0 Radius=0.5
  constraints (10):
    c: Coincident(g0,g-1)
    c: PointOnObject(g-3,g0)
    c: Coincident(g1,g0)
    c: Coincident(g2,g0)
    c: Angle(g2,g1) = 0.1309
    c: Coincident(g1,g-3)
    c: PointOnObject(g3,g2)
    c: Diameter(g3) = 1
    c: PointOnObject(g2,g0)
    c: Distance(g3,g2) = 0.2
FEATURE [PartDesign::SubShapeBinder] Binder072
  BindCopyOnChange = 0
  BindMode = 0
  ClaimChildren = false
  Context = -> Body013 [Binder072.]
  Fuse = false
  MakeFace = true
  Offset = -0.15
  OffsetFill = false
  OffsetIntersection = false
  OffsetJoinType = 0
  OffsetOpenResult = false
  PartialLoad = false
  Relative = true
  Support = -> [Body005[Groove001.Sketch123.]]
  _Version = 2
FEATURE [PartDesign::SubShapeBinder] Binder073
  BindCopyOnChange = 0
  BindMode = 0
  ClaimChildren = false
  Context = -> Body013 [Binder073.]
  Fuse = false
  MakeFace = false
  OffsetFill = false
  OffsetIntersection = false
  OffsetJoinType = 0
  OffsetOpenResult = false
  PartialLoad = false
  Relative = true
  Support = -> [Body[Sketch114.]]
  _Version = 2
FEATURE [Sketcher::SketchObject] Sketch127
  ArcFitTolerance = 0
  AttachmentOffset = pos=(0,0,-17) rot=(0,0,1;0rad)
  AttachmentSupport = -> [XY_Plane013]
  ExternalGeometry = -> [Binder073]
  FullyConstrained = true
  MakeInternals = false
  MapMode = 5
  Placement = pos=(0,0,-17) rot=(0,0,1;0rad)
  expr: .AttachmentOffset.Base.z = -Spreadsheet.mountH
  sketch-geometry (6):
    g0: ArcOfCircle CenterX=-7.1e-15 CenterY=1.3e-15 CenterZ=0 NormalX=0 NormalY=0 NormalZ=1 AngleXU=0 Radius=38 StartAngle=3.92699 EndAngle=8.63938
    g1: ArcOfCircle CenterX=-7.1e-15 CenterY=1.3e-15 CenterZ=0 NormalX=0 NormalY=0 NormalZ=1 AngleXU=0 Radius=31 StartAngle=3.92699 EndAngle=8.63938
    g2: LineSegment [constr] StartX=-26.8701 StartY=26.8701 StartZ=0 EndX=-1.07e-14 EndY=0 EndZ=0
    g3: LineSegment [constr] StartX=-7.1e-15 StartY=1.3e-15 StartZ=0 EndX=-26.8701 EndY=-26.8701 EndZ=0
    g4: LineSegment StartX=-21.9203 StartY=21.9203 StartZ=0 EndX=-26.8701 EndY=26.8701 EndZ=0
    g5: LineSegment StartX=-21.9203 StartY=-21.9203 StartZ=0 EndX=-26.8701 EndY=-26.8701 EndZ=0
  constraints (16):
    c: Coincident(g0,g-1)
    c: Equal(g0,g-3)
    c: Vertical(g0,g0)
    c: Angle(g0) = 4.71239
    c: Coincident(g1,g0)
    c: Coincident(g2,g0)
    c: Coincident(g2,g0)
    c: Coincident(g3,g0)
    c: Coincident(g3,g0)
    c: PointOnObject(g1,g2)
    c: PointOnObject(g1,g3)
    c: Coincident(g4,g1)
    c: Coincident(g4,g0)
    c: Coincident(g5,g1)
    c: Coincident(g5,g0)
    c: Distance(g4) = 7
FEATURE [PartDesign::Pad] Pad030
  Direction = (0,0,1)
  Length = 2
  Length2 = 10
  Profile = -> Sketch127
  ReferenceAxis = -> Sketch127 [N_Axis]
  Reversed = true
  Suppressed = false
  Type = 0
FEATURE [Sketcher::SketchObject] Sketch128
  ArcFitTolerance = 0
  AttachmentSupport = -> [YZ_Plane013]
  ExternalGeometry = -> [Binder072]
  FullyConstrained = true
  MakeInternals = false
  MapMode = 5
  Placement = pos=(0,0,0) rot=(0.57735,0.57735,0.57735;2.0944rad)
  sketch-geometry (11):
    g0: LineSegment StartX=33.1061 StartY=-16.1061 StartZ=0 EndX=33.15 EndY=-12.2413 EndZ=0
    g1: LineSegment StartX=33.15 StartY=-12.2413 StartZ=0 EndX=35 EndY=-11.1732 EndZ=0
    g2: LineSegment StartX=35 StartY=-11.1732 StartZ=0 EndX=36.85 EndY=-12.2413 EndZ=0
    g3: LineSegment StartX=36.85 StartY=-12.2413 StartZ=0 EndX=36.85 EndY=-13.0926 EndZ=0
    g4: LineSegment StartX=36.85 StartY=-13.0926 StartZ=0 EndX=34.85 EndY=-15.1547 EndZ=0
    g5: LineSegment StartX=34.85 StartY=-15.1547 StartZ=0 EndX=34.8939 EndY=-16.1061 EndZ=0
    g6: LineSegment StartX=34.8939 StartY=-16.1061 StartZ=0 EndX=35.6379 EndY=-16.85 EndZ=0
    g7: LineSegment StartX=35.6379 StartY=-16.85 StartZ=0 EndX=35.8379 EndY=-17.05 EndZ=0
    g8: LineSegment StartX=35.8379 StartY=-17.05 StartZ=0 EndX=32.1621 EndY=-17.05 EndZ=0
    g9: LineSegment StartX=32.1621 StartY=-17.05 StartZ=0 EndX=32.3621 EndY=-16.85 EndZ=0
    g10: LineSegment StartX=32.3621 StartY=-16.85 StartZ=0 EndX=33.1061 EndY=-16.1061 EndZ=0
  constraints (24):
    c: Coincident(g8,g9)
    c: Coincident(g9,g10)
    c: Coincident(g0,g10)
    c: Coincident(g0,g1)
    c: Coincident(g4,g5)
    c: Coincident(g5,g6)
    c: Coincident(g1,g2)
    c: Coincident(g6,g7)
    c: Coincident(g7,g8)
    c: Coincident(g3,g4)
    c: Coincident(g2,g3)
    c: Coincident(g1,g-3)
    c: Coincident(g2,g-4)
    c: Coincident(g3,g-5)
    c: Coincident(g4,g-6)
    c: Coincident(g5,g-7)
    c: Coincident(g6,g-10)
    c: Coincident(g0,g-9)
    c: Coincident(g9,g-8)
    c: Parallel(g6,g7)
    c: Parallel(g10,g9)
    c: DistanceY(g7,g6) = 0.2
    c: Horizontal(g8)
    c: Coincident(g0,g-11)
FEATURE [PartDesign::Revolution] Revolution005
  Angle = 15
  Angle2 = 60
  Axis = (1e-16,1e-16,1)
  Base = (0,0,0)
  BaseFeature = -> Pad030
  Profile = -> Sketch128
  ReferenceAxis = -> Z_Axis013
  Refine = true
  Reversed = true
  Suppressed = false
  Type = 0
FEATURE [Sketcher::SketchObject] Sketch126
  ArcFitTolerance = 0
  AttachmentOffset = pos=(0,0,-17) rot=(0,0,1;0rad)
  AttachmentSupport = -> [XY_Plane013]
  ExternalGeometry = -> [Sketch128]
  FullyConstrained = true
  MakeInternals = false
  MapMode = 5
  Placement = pos=(0,0,-17) rot=(0,0,1;0rad)
  expr: .AttachmentOffset.Base.z = -Spreadsheet.mountH
  sketch-geometry (5):
    g0: Circle [constr] CenterX=0 CenterY=0 CenterZ=0 NormalX=0 NormalY=0 NormalZ=1 AngleXU=0 Radius=36.85
    g1: Circle CenterX=4.85557 CenterY=36.8817 CenterZ=0 NormalX=0 NormalY=0 NormalZ=1 AngleXU=0 Radius=0.55
    g2: LineSegment [constr] StartX=0 StartY=0 StartZ=0 EndX=1.09e-14 EndY=36.85 EndZ=0
    g3: LineSegment [constr] StartX=4.80989 StartY=36.5347 StartZ=0 EndX=0 EndY=0 EndZ=0
    g4: LineSegment [constr] StartX=4.85557 StartY=36.8817 StartZ=0 EndX=4.80989 EndY=36.5347 EndZ=0
  constraints (12):
    c: Coincident(g0,g-1)
    c: Diameter(g1) = 1.1
    c: Coincident(g2,g0)
    c: PointOnObject(g2,g0)
    c: Coincident(g2,g-3)
    c: Coincident(g3,g0)
    c: Angle(g3,g2) = 0.1309
    c: PointOnObject(g3,g0)
    c: Coincident(g4,g1)
    c: Coincident(g4,g3)
    c: Parallel(g4,g3)
    c: Distance(g4) = 0.35
FEATURE [PartDesign::Pocket] Pocket022
  BaseFeature = -> Revolution005
  Direction = (0,0,-1)
  Length = 5
  Length2 = 5
  Profile = -> Sketch126
  ReferenceAxis = -> Sketch126 [N_Axis]
  Refine = true
  Reversed = true
  Suppressed = false
  Type = 1
FEATURE [Sketcher::SketchObject] Sketch129
  ArcFitTolerance = 0
  AttachmentOffset = pos=(0,0,-19) rot=(0,0,1;0rad)
  AttachmentSupport = -> [XY_Plane013]
  ExternalGeometry = -> [Sketch127]
  FullyConstrained = true
  MakeInternals = false
  MapMode = 5
  Placement = pos=(0,0,-19) rot=(0,0,1;0rad)
  expr: .AttachmentOffset.Base.z = -Spreadsheet.mountH - 2 mm
  sketch-geometry (5):
    g0: LineSegment StartX=-21.9203 StartY=21.9203 StartZ=0 EndX=-26.8701 EndY=26.8701 EndZ=0
    g1: LineSegment StartX=5.255e-13 StartY=38 StartZ=0 EndX=4.287e-13 EndY=31 EndZ=0
    g2: LineSegment [constr] StartX=5.255e-13 StartY=38 StartZ=0 EndX=0 EndY=0 EndZ=0
    g3: ArcOfCircle CenterX=0 CenterY=0 CenterZ=0 NormalX=0 NormalY=0 NormalZ=1 AngleXU=0 Radius=38 StartAngle=1.5708 EndAngle=2.35619
    g4: ArcOfCircle CenterX=0 CenterY=0 CenterZ=0 NormalX=0 NormalY=0 NormalZ=1 AngleXU=0 Radius=31 StartAngle=1.5708 EndAngle=2.35619
  constraints (12):
    c: Coincident(g0,g-4)
    c: Coincident(g0,g-5)
    c: Angle(g1,g0) = 0.785398
    c: Coincident(g2,g1)
    c: Coincident(g2,g-5)
    c: PointOnObject(g1,g2)
    c: Coincident(g3,g2)
    c: Coincident(g3,g1)
    c: Coincident(g3,g0)
    c: Coincident(g4,g3)
    c: Coincident(g4,g1)
    c: Coincident(g4,g0)
FEATURE [Sketcher::SketchObject] Sketch130
  ArcFitTolerance = 0
  AttachmentOffset = pos=(0,0,-29) rot=(0,0,1;0rad)
  AttachmentSupport = -> [XY_Plane013]
  ExternalGeometry = -> [Sketch129]
  FullyConstrained = false
  MakeInternals = false
  MapMode = 5
  Placement = pos=(0,0,-29) rot=(0,0,1;0rad)
  expr: .AttachmentOffset.Base.z = -Spreadsheet.mountH - 2 mm - 10 mm
  sketch-geometry (3):
    g0: Circle CenterX=-13.1828 CenterY=31.8262 CenterZ=0 NormalX=0 NormalY=0 NormalZ=1 AngleXU=0 Radius=3.5
    g1: LineSegment [constr] StartX=-13.1828 StartY=31.8262 StartZ=0 EndX=-21.9203 EndY=21.9203 EndZ=0
    g2: LineSegment [constr] StartX=-13.1828 StartY=31.8262 StartZ=0 EndX=4.281e-13 EndY=31 EndZ=0
  constraints (6):
    c: Coincident(g1,g0)
    c: Coincident(g1,g-4)
    c: Coincident(g2,g0)
    c: Coincident(g2,g-4)
    c: Equal(g2,g1)
    c: Diameter(g0) = 7
FEATURE [Sketcher::SketchObject] Sketch131
  ArcFitTolerance = 0
  AttachmentOffset = pos=(0,0,-92) rot=(0,0,1;0rad)
  AttachmentSupport = -> [XY_Plane013]
  ExternalGeometry = -> [Sketch130,Sketch127]
  FullyConstrained = true
  MakeInternals = false
  MapMode = 5
  Placement = pos=(0,0,-92) rot=(0,0,1;0rad)
  expr: .AttachmentOffset.Base.z = -Spreadsheet.mountH - 5 mm - 70 mm
  sketch-geometry (5):
    g0: Circle [constr] CenterX=0 CenterY=0 CenterZ=0 NormalX=0 NormalY=0 NormalZ=1 AngleXU=0 Radius=58
    g1: LineSegment [constr] StartX=0 StartY=58 StartZ=0 EndX=0 EndY=38 EndZ=0
    g2: Circle CenterX=-41.0122 CenterY=41.0122 CenterZ=0 NormalX=0 NormalY=0 NormalZ=1 AngleXU=0 Radius=3.5
    g3: LineSegment [constr] StartX=-13.1828 StartY=31.8262 StartZ=0 EndX=0 EndY=0 EndZ=0
    g4: LineSegment [constr] StartX=0 StartY=0 StartZ=0 EndX=-41.0122 EndY=41.0122 EndZ=0
  constraints (13):
    c: Coincident(g0,g-1)
    c: PointOnObject(g2,g0)
    c: PointOnObject(g1,g0)
    c: PointOnObject(g1,g-4)
    c: PointOnObject(g1,g-2)
    c: PointOnObject(g1,g-2)
    c: DistanceY(g1,g1) = 20
    c: Equal(g-3,g2)
    c: Coincident(g3,g-3)
    c: Coincident(g3,g0)
    c: Coincident(g4,g0)
    c: Coincident(g4,g2)
    c: Angle(g3,g4) = 0.392699
FEATURE [PartDesign::PolarPattern] PolarPattern002
  Angle = 90
  Axis = -> Sketch129 [N_Axis]
  Mode = 0
  Occurrences = 3
  Offset = 120
  Reversed = true
  Suppressed = false
  TransformMode = 0
FEATURE [PartDesign::Mirrored] Mirrored
  MirrorPlane = -> XZ_Plane013
  Suppressed = false
  TransformMode = 0
FEATURE [Sketcher::SketchObject] Sketch132
  ArcFitTolerance = 0
  AttachmentOffset = pos=(0,0,-92) rot=(0,0,1;0rad)
  AttachmentSupport = -> [XY_Plane013]
  ExternalGeometry = -> [Sketch131]
  FullyConstrained = true
  MakeInternals = false
  MapMode = 5
  Placement = pos=(0,0,-92) rot=(0,0,1;0rad)
  expr: .AttachmentOffset.Base.z = -Spreadsheet.mountH - 5 mm - 70 mm
  sketch-geometry (6):
    g0: ArcOfCircle CenterX=41.0122 CenterY=41.0122 CenterZ=0 NormalX=0 NormalY=0 NormalZ=1 AngleXU=0 Radius=3.5 StartAngle=3.92699 EndAngle=7.06858
    g1: ArcOfCircle CenterX=-7.1e-15 CenterY=0 CenterZ=0 NormalX=0 NormalY=0 NormalZ=1 AngleXU=0 Radius=54.5 StartAngle=0.785398 EndAngle=5.49779
    g2: ArcOfCircle CenterX=-7.1e-15 CenterY=0 CenterZ=0 NormalX=0 NormalY=0 NormalZ=1 AngleXU=0 Radius=61.5 StartAngle=0.785398 EndAngle=5.49779
    g3: ArcOfCircle CenterX=41.0122 CenterY=-41.0122 CenterZ=0 NormalX=0 NormalY=0 NormalZ=1 AngleXU=0 Radius=3.5 StartAngle=5.49779 EndAngle=8.63938
    g4: LineSegment [constr] StartX=-41.0122 StartY=41.0122 StartZ=0 EndX=-7.1e-15 EndY=0 EndZ=0
    g5: LineSegment [constr] StartX=-7.1e-15 StartY=0 StartZ=0 EndX=41.0122 EndY=41.0122 EndZ=0
  constraints (14):
    c: Coincident(g1,g-1)
    c: Coincident(g2,g1)
    c: Tangent(g3,g1) = 1.5708
    c: Tangent(g1,g0) = 1.5708
    c: Tangent(g2,g0) = -1.5708
    c: Tangent(g3,g2) = -1.5708
    c: Vertical(g3,g0)
    c: Coincident(g4,g-3)
    c: Coincident(g4,g1)
    c: Coincident(g5,g1)
    c: Angle(g5,g4) = 1.5708
    c: Coincident(g0,g5)
    c: Equal(g4,g5)
    c: Equal(g-3,g0)
FEATURE [PartDesign::Fillet] Fillet003
  Base = -> Pocket022 [Edge51,Edge46,Edge20,Edge34]
  BaseFeature = -> Pocket022
  Radius = 0.5
  SupportTransform = false
  Suppressed = false
  UseAllEdges = false
  expr: Radius = 0.5 mm
FEATURE [PartDesign::PolarPattern] PolarPattern001
  Angle = 180
  Axis = -> Z_Axis013
  BaseFeature = -> Fillet003
  Mode = 0
  Occurrences = 3
  Offset = 120
  Originals = -> [Revolution005,Pocket022,Fillet003]
  Reversed = true
  Suppressed = false
  TransformMode = 0
FEATURE [PartDesign::AdditiveLoft] AdditiveLoft
  BaseFeature = -> PolarPattern001
  Closed = false
  Profile = -> Sketch129
  Ruled = true
  Sections = -> [Sketch130,Sketch131]
  Suppressed = false
FEATURE [PartDesign::MultiTransform] MultiTransform
  BaseFeature = -> AdditiveLoft
  Originals = -> [AdditiveLoft]
  Suppressed = false
  TransformMode = 0
  Transformations = -> [PolarPattern002,Mirrored]
FEATURE [PartDesign::Pad] Pad032
  BaseFeature = -> MultiTransform
  Direction = (0,0,1)
  Length = 2
  Length2 = 10
  Profile = -> Sketch132
  ReferenceAxis = -> Sketch132 [N_Axis]
  Reversed = true
  Suppressed = false
  Type = 0
FEATURE [PartDesign::Body] Body013  label="Leg"
  AllowCompound = false
  Group = -> [Binder073,Pad030,Binder072,Sketch128,Revolution005,Sketch126,Pocket022,Fillet003,Sketch127,PolarPattern001,Sketch129,Sketch130,Sketch131,AdditiveLoft,MultiTransform,PolarPattern002,Mirrored,Sketch132,Pad032]
  Origin = -> Origin013
  Tip = -> Pad032
FEATURE [PartDesign::Pocket] Pocket023
  BaseFeature = -> Pad021
  Direction = (0,0,-1)
  Length = 5
  Length2 = 5
  Profile = -> Binder024 [Face1]
  Suppressed = false
  Type = 1
FEATURE [PartDesign::Pocket] Pocket024
  BaseFeature = -> Pocket023
  Direction = (0,0,-1)
  Length = 5
  Length2 = 5
  Profile = -> Binder025
  Suppressed = false
  Type = 1
FEATURE [PartDesign::Pocket] Pocket005
  BaseFeature = -> Pocket024
  Direction = (0,0,-1)
  Length = 3
  Length2 = 5
  Profile = -> Sketch081
  ReferenceAxis = -> Sketch081 [N_Axis]
  Suppressed = false
  Type = 0
FEATURE [Sketcher::SketchObject] Sketch135
  ArcFitTolerance = 0
  AttachmentOffset = pos=(0,0,-3) rot=(0,0,1;0rad)
  AttachmentSupport = -> [XY_Plane005]
  FullyConstrained = false
  MakeInternals = false
  MapMode = 5
  Placement = pos=(0,0,-3) rot=(0,0,1;0rad)
  expr: Constraints[15] = Spreadsheet.tol
  sketch-geometry (7):
    g0: LineSegment StartX=13.3787 StartY=13.3787 StartZ=0 EndX=18.3978 EndY=14.7235 EndZ=0
    g1: LineSegment StartX=18.3978 StartY=14.7235 StartZ=0 EndX=14.7235 EndY=18.3978 EndZ=0
    g2: LineSegment StartX=14.7235 StartY=18.3978 StartZ=0 EndX=13.3787 EndY=13.3787 EndZ=0
    g3: Circle [constr] CenterX=15.5 CenterY=15.5 CenterZ=0 NormalX=0 NormalY=0 NormalZ=1 AngleXU=0 Radius=3
    g4: LineSegment [constr] StartX=15.5 StartY=15.5 StartZ=0 EndX=0 EndY=0 EndZ=0
    g5: Circle CenterX=15.5 CenterY=15.5 CenterZ=0 NormalX=0 NormalY=0 NormalZ=1 AngleXU=0 Radius=3.1
    g6: LineSegment [constr] StartX=18.3978 StartY=14.7235 StartZ=0 EndX=18.4944 EndY=14.6977 EndZ=0
  constraints (16):
    c: Coincident(g0,g1)
    c: Coincident(g1,g2)
    c: Coincident(g2,g0)
    c: Equal(g0,g1)
    c: Equal(g0,g2)
    c: PointOnObject(g0,g3)
    c: PointOnObject(g1,g3)
    c: PointOnObject(g2,g3)
    c: Coincident(g4,g3)
    c: Coincident(g4,g-1)
    c: PointOnObject(g0,g4)
    c: Coincident(g5,g3)
    c: Coincident(g6,g0)
    c: PointOnObject(g6,g5)
    c: Perpendicular(g5,g6)
    c: Distance(g6) = 0.1
FEATURE [PartDesign::Pad] Pad033
  BaseFeature = -> Pocket005
  Direction = (0,0,1)
  Length = 0.2
  Length2 = 10
  Profile = -> Sketch135
  ReferenceAxis = -> Sketch135 [N_Axis]
  Suppressed = false
  Type = 0
FEATURE [Sketcher::SketchObject] Sketch136
  ArcFitTolerance = 0
  AttachmentSupport = -> [XY_Plane005]
  ExternalGeometry = -> [Binder021]
  FullyConstrained = true
  MakeInternals = false
  MapMode = 5
  sketch-geometry (1):
    g0: Circle CenterX=15.5 CenterY=15.5 CenterZ=0 NormalX=0 NormalY=0 NormalZ=1 AngleXU=0 Radius=1.5
  constraints (2):
    c: Coincident(g0,g-3)
    c: Equal(g0,g-3)
FEATURE [PartDesign::Pocket] Pocket026
  BaseFeature = -> Pad033
  Direction = (0,0,-1)
  Length = 5
  Length2 = 5
  Profile = -> Sketch136
  ReferenceAxis = -> Sketch136 [N_Axis]
  Suppressed = false
  Type = 1
FEATURE [PartDesign::PolarPattern] PolarPattern003
  Angle = 360
  Axis = -> Sketch081 [N_Axis]
  BaseFeature = -> Pocket026
  Mode = 0
  Occurrences = 4
  Offset = 120
  Originals = -> [Pocket005,Pad033,Pocket026]
  Suppressed = false
  TransformMode = 0
FEATURE [PartDesign::Pocket] Pocket017
  BaseFeature = -> PolarPattern003
  Direction = (-1,0,0)
  Length = 5
  Length2 = 5
  Profile = -> Sketch112
  ReferenceAxis = -> Sketch112 [N_Axis]
  Refine = true
  Reversed = true
  Suppressed = false
  Type = 1
FEATURE [PartDesign::Pocket] Pocket
  BaseFeature = -> Pocket017
  Direction = (0,0,-1)
  Length = 5
  Length2 = 5
  Midplane = true
  Profile = -> Sketch116
  ReferenceAxis = -> Sketch116 [N_Axis]
  Refine = true
  Suppressed = false
  Type = 1
FEATURE [PartDesign::Pocket] Pocket019
  BaseFeature = -> Pocket
  Direction = (0,0,-1)
  Length = 2.2
  Length2 = 5
  Profile = -> Binder069
  Suppressed = false
  Type = 0
FEATURE [PartDesign::Groove] Groove001
  Angle = 15
  Angle2 = 60
  Axis = (1e-16,1e-16,1)
  Base = (0,0,0)
  BaseFeature = -> Pocket019
  Profile = -> Sketch123
  ReferenceAxis = -> Z_Axis005
  Reversed = true
  Suppressed = false
  Type = 0
FEATURE [PartDesign::Groove] Groove002
  Angle = 30
  Angle2 = 60
  Axis = (1e-16,1e-16,1)
  Base = (0,0,0)
  BaseFeature = -> Groove001
  Profile = -> Sketch124
  ReferenceAxis = -> Z_Axis005
  Suppressed = false
  Type = 0
FEATURE [PartDesign::Pad] Pad031
  BaseFeature = -> Groove002
  Direction = (0,0,1)
  Length = 10
  Length2 = 10
  Profile = -> Sketch125
  ReferenceAxis = -> Sketch125 [N_Axis]
  Suppressed = false
  Type = 0
FEATURE [PartDesign::PolarPattern] PolarPattern
  Angle = 180
  Axis = -> Z_Axis005
  BaseFeature = -> Pad031
  Mode = 0
  Occurrences = 3
  Offset = 120
  Originals = -> [Groove001,Groove002,Pad031]
  Suppressed = false
  TransformMode = 0
FEATURE [Sketcher::SketchObject] Sketch137
  ArcFitTolerance = 1e-06
  AttachmentSupport = -> [XY_Plane005]
  ExternalGeometry = -> [Binder069]
  FullyConstrained = true
  MakeInternals = false
  MapMode = 5
  sketch-geometry (15):
    g0: LineSegment StartX=-18.6877 StartY=26.3263 StartZ=0 EndX=-17.1964 EndY=28.4561 EndZ=0
    g1: LineSegment StartX=-17.1964 StartY=28.4561 StartZ=0 EndX=-19.3262 EndY=29.9474 EndZ=0
    g2: LineSegment StartX=-19.3262 StartY=29.9474 StartZ=0 EndX=-18.7526 EndY=30.7665 EndZ=0
    g3: LineSegment StartX=-18.7526 StartY=30.7665 StartZ=0 EndX=-16.6228 EndY=29.2752 EndZ=0
    g4: LineSegment StartX=-16.6228 StartY=29.2752 StartZ=0 EndX=-15.1315 EndY=31.405 EndZ=0
    g5: LineSegment StartX=-15.1315 StartY=31.405 StartZ=0 EndX=-14.3123 EndY=30.8314 EndZ=0
    g6: LineSegment StartX=-14.3123 StartY=30.8314 StartZ=0 EndX=-15.8036 EndY=28.7016 EndZ=0
    g7: LineSegment StartX=-15.8036 StartY=28.7016 StartZ=0 EndX=-13.6739 EndY=27.2103 EndZ=0
    g8: LineSegment StartX=-13.6739 StartY=27.2103 StartZ=0 EndX=-14.2474 EndY=26.3912 EndZ=0
    g9: LineSegment StartX=-14.2474 StartY=26.3912 StartZ=0 EndX=-16.3772 EndY=27.8825 EndZ=0
    g10: LineSegment StartX=-16.3772 StartY=27.8825 StartZ=0 EndX=-17.8685 EndY=25.7527 EndZ=0
    g11: LineSegment StartX=-17.8685 StartY=25.7527 StartZ=0 EndX=-18.6877 EndY=26.3263 EndZ=0
    g12: LineSegment [constr] StartX=-17.1964 StartY=28.4561 StartZ=0 EndX=-15.8036 EndY=28.7016 EndZ=0
    g13: LineSegment [constr] StartX=-16.6228 StartY=29.2752 StartZ=0 EndX=-16.3772 EndY=27.8825 EndZ=0
    g14: LineSegment [constr] StartX=-16.5 StartY=28.5788 StartZ=0 EndX=0 EndY=0 EndZ=0
  constraints (42):
    c: Coincident(g0,g1)
    c: Coincident(g1,g2)
    c: Coincident(g2,g3)
    c: Coincident(g3,g4)
    c: Coincident(g4,g5)
    c: Coincident(g5,g6)
    c: Coincident(g6,g7)
    c: Coincident(g7,g8)
    c: Coincident(g8,g9)
    c: Coincident(g9,g10)
    c: Coincident(g10,g11)
    c: Coincident(g11,g0)
    c: Perpendicular(g0,g1)
    c: Perpendicular(g4,g3)
    c: Perpendicular(g7,g6)
    c: Perpendicular(g10,g9)
    c: Parallel(g1,g3)
    c: Parallel(g9,g7)
    c: Equal(g3,g1)
    c: Equal(g1,g4)
    c: Equal(g4,g6)
    c: Equal(g6,g7)
    c: Equal(g7,g9)
    c: Equal(g9,g10)
    c: Equal(g10,g0)
    c: Equal(g5,g2)
    c: Equal(g2,g11)
    c: Equal(g11,g8)
    c: Perpendicular(g3,g2)
    c: Perpendicular(g5,g4)
    c: Perpendicular(g11,g0)
    c: Distance(g2) = 1
    c: Coincident(g12,g0)
    c: Coincident(g12,g6)
    c: Coincident(g13,g3)
    c: Coincident(g13,g9)
    c: PointOnObject(g-3,g12)
    c: Coincident(g14,g-6)
    c: Coincident(g14,g-1)
    c: PointOnObject(g14,g12)
    c: PointOnObject(g14,g13)
    c: Tangent(g2,g-6)
FEATURE [PartDesign::Pocket] Pocket027
  BaseFeature = -> PolarPattern
  Direction = (0,0,-1)
  Length = 5
  Length2 = 5
  Profile = -> Sketch137
  ReferenceAxis = -> Sketch137 [N_Axis]
  Suppressed = false
  Type = 2
FEATURE [PartDesign::Fillet] Fillet
  Base = -> Pocket027 [Edge133,Edge124,Edge114,Edge105]
  BaseFeature = -> Pocket027
  Radius = 1
  SupportTransform = false
  Suppressed = false
  UseAllEdges = false
FEATURE [PartDesign::PolarPattern] PolarPattern004
  Angle = 360
  Axis = -> Z_Axis005
  BaseFeature = -> Fillet
  Mode = 1
  Occurrences = 7
  Offset = 40
  Originals = -> [Fillet,Pocket027]
  Reversed = true
  Suppressed = false
  TransformMode = 0
FEATURE [PartDesign::Body] Body005  label="motorMount"
  AllowCompound = false
  Group = -> [Binder067,Pad021,Binder021,Binder024,Pocket023,Binder025,Pocket024,Pocket005,Pad033,Sketch136,Pocket026,PolarPattern003,Sketch081,Sketch112,Pocket017,Sketch135,Sketch116,Pocket,Binder069,Pocket019,Groove001,Groove002,Pad031,Sketch123,Sketch124,Sketch125,PolarPattern,Sketch137,Pocket027,Fillet,PolarPattern004]
  Origin = -> Origin005
  Tip = -> PolarPattern004
FEATURE [PartDesign::Pad] Pad034
  BaseFeature = -> Pad024
  Direction = (1,0,0.7)
  Length = 56
  Length2 = 10
  Midplane = true
  Profile = -> Binder058
  Suppressed = false
  Type = 0
  UseCustomVector = true
  expr: Length = 2 * Spreadsheet.bodyR
FEATURE [PartDesign::Pocket] Pocket021
  BaseFeature = -> Pad034
  Direction = (1,0,0.7)
  Length = 72
  Length2 = 5
  Profile = -> Sketch122
  ReferenceAxis = -> Sketch122 [N_Axis]
  Refine = true
  Suppressed = false
  Type = 0
  UseCustomVector = true
  expr: Length = 2 * Spreadsheet.bodyR + 16 mm
FEATURE [PartDesign::Body] Body012  label="BodyNegative"
  AllowCompound = false
  Group = -> [Binder058,Binder070,Pad024,Sketch122,Pad034,Pocket021]
  Origin = -> Origin012
  Tip = -> Pocket021
FEATURE [PartDesign::SubShapeBinder] Binder074  label="HoleBinder"
  BindCopyOnChange = 0
  BindMode = 0
  ClaimChildren = false
  Context = -> Body001 [Binder074.]
  Fuse = false
  MakeFace = true
  Offset = 2
  OffsetFill = false
  OffsetIntersection = false
  OffsetJoinType = 0
  OffsetOpenResult = false
  PartialLoad = false
  Relative = true
  Support = -> [Body[Sketch103.]]
  _Version = 2
  expr: Offset = Spreadsheet.wallThickness
FEATURE [PartDesign::Pad] Pad035
  BaseFeature = -> Revolution004
  Direction = (1,0,0.7)
  Length = 28
  Length2 = 10
  Placement = pos=(0,0,0) rot=(1,1,1;2.0944rad)
  Profile = -> Binder074
  Suppressed = false
  Type = 0
  UseCustomVector = true
  expr: Length = Spreadsheet.bodyR
FEATURE [PartDesign::Pad] Pad
  BaseFeature = -> Pad035
  Direction = (1,0,0.7)
  Length = 10
  Length2 = 10
  Placement = pos=(0,0,0) rot=(1,1,1;2.0944rad)
  Profile = -> Binder074
  Reversed = true
  Suppressed = false
  Type = 0
  UseCustomVector = true
FEATURE [PartDesign::Boolean] Boolean
  BaseFeature = -> Pad
  Group = -> [Binder060]
  Refine = true
  Suppressed = false
  Type = 1
  UsePlacement = false
FEATURE [PartDesign::Fillet] Fillet004
  Base = -> Boolean [Edge22,Edge16]
  BaseFeature = -> Boolean
  Radius = 4
  SupportTransform = false
  Suppressed = false
  UseAllEdges = false
FEATURE [PartDesign::Pocket] Pocket009
  BaseFeature = -> Fillet004
  Direction = (0,0,-1)
  Length = 5
  Length2 = 5
  Profile = -> Binder032
  Reversed = true
  Suppressed = false
  Type = 1
FEATURE [PartDesign::Groove] Groove
  Angle = 360
  Angle2 = 60
  Axis = (0,2e-16,1)
  Base = (0,0,0)
  BaseFeature = -> Pocket009
  Profile = -> Sketch088
  ReferenceAxis = -> Sketch088 [V_Axis]
  Suppressed = false
  Type = 0
FEATURE [PartDesign::SubtractiveHelix] SubtractiveHelix003
  Angle = 0
  Axis = (1e-16,1e-16,1)
  Base = (0,0,0)
  BaseFeature = -> Groove
  Growth = 0
  HasBeenEdited = true
  Height = 9
  LeftHanded = false
  Mode = 0
  Outside = false
  Pitch = 3
  Profile = -> Binder038 [Face1]
  ReferenceAxis = -> Z_Axis001
  Suppressed = false
  Turns = 3
FEATURE [PartDesign::Pocket] Pocket018
  BaseFeature = -> SubtractiveHelix003
  Direction = (0,0,-1)
  Length = 2.2
  Length2 = 5
  Profile = -> Binder068
  Reversed = true
  Suppressed = false
  Type = 0
FEATURE [PartDesign::Body] Body001  label="Body"
  AllowCompound = false
  Group = -> [Binder,Revolution004,Binder074,Pad035,Pad,Binder066,Boolean,Fillet004,Binder032,Pocket009,Binder033,Sketch088,Groove,Binder038,SubtractiveHelix003,Binder068,Pocket018,Sketch118]
  Origin = -> Origin001
  Tip = -> Pocket018
FEATURE [PartDesign::Chamfer] Chamfer
  Angle = 45
  Base = -> Pad007 [Edge3]
  BaseFeature = -> Pad007
  ChamferType = 0
  FlipDirection = false
  Size = 1
  Size2 = 1
  SupportTransform = false
  Suppressed = false
  UseAllEdges = false
FEATURE [PartDesign::Body] Body002  label="worm"
  AllowCompound = false
  Group = -> [Binder005,Binder006,Pad001,AdditiveHelix,Binder031,Sketch086,Pocket008,Sketch087,Pad007,Chamfer]
  Origin = -> Origin002
  Tip = -> Chamfer
